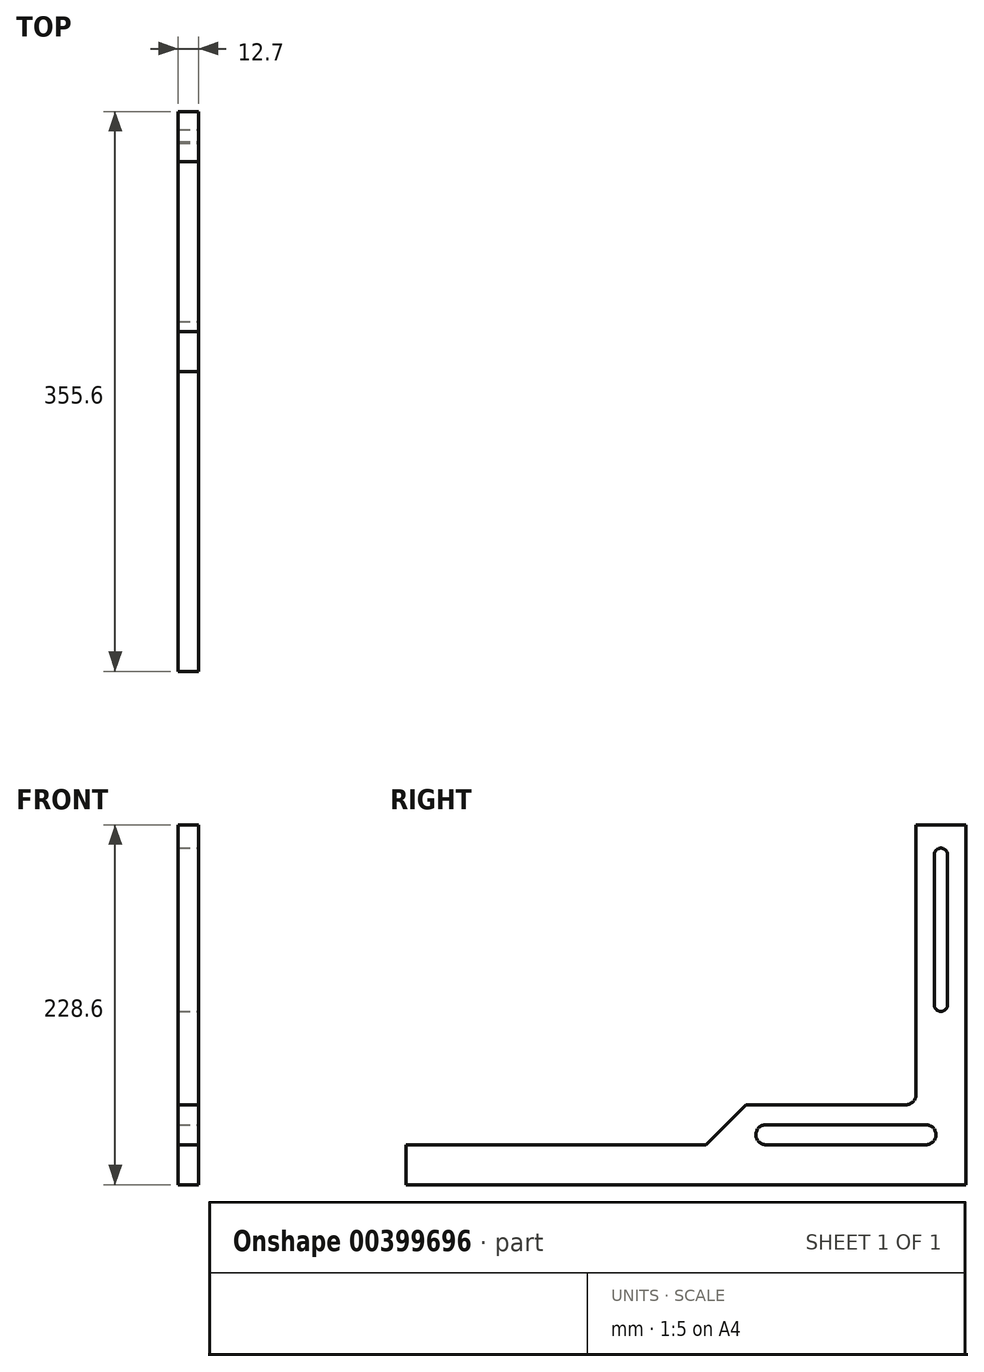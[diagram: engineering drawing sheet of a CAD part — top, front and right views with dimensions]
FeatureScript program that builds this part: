
annotation { "Feature Type Name" : "Feature", "Feature Type Description" : "" }
export const myFeature = defineFeature(function(context is Context, id is Id, definition is map)
    precondition{}
    {
        {
            var Q0;
            Q0=qCreatedBy(makeId("Right.planeOp"),FACE);
            var sketch = newSketch(context, id + "F0", { "sketchPlane" : qUnion([Q0])});
            skLineSegment(sketch, "E0.bottom", {"start": v(-177.8, 25.4) * mm, "end": v(177.8, 25.4) * mm});
            skLineSegment(sketch, "E0.top", {"start": v(-177.8, 0) * mm, "end": v(177.8, 0) * mm});
            skLineSegment(sketch, "E0.left", {"start": v(-177.8, 25.4) * mm, "end": v(-177.8, 0) * mm});
            skLineSegment(sketch, "E0.right", {"start": v(177.8, 25.4) * mm, "end": v(177.8, 0) * mm});
            skLineSegment(sketch, "E1.bottom", {"start": v(177.8, 0) * mm, "end": v(146.05, 0) * mm});
            skLineSegment(sketch, "E1.top", {"start": v(177.8, 228.6) * mm, "end": v(146.05, 228.6) * mm});
            skLineSegment(sketch, "E1.left", {"start": v(177.8, 0) * mm, "end": v(177.8, 228.6) * mm});
            skLineSegment(sketch, "E1.right", {"start": v(146.05, 57.15) * mm, "end": v(146.05, 228.6) * mm});
            skLineSegment(sketch, "E2", {"start": v(139.7, 50.8) * mm, "end": v(38.1, 50.8) * mm});
            skLineSegment(sketch, "E3", {"start": v(38.1, 50.8) * mm, "end": v(12.7, 25.4) * mm});
            skPoint(sketch, "E4.newPointA", {"position": v(146.05, 50.8) * mm});
            skArc(sketch, "E4.filletArc", {"start": v(139.7, 50.8) * mm, "mid": v(144.2, 52.66) * mm, "end": v(146.05, 57.15) * mm});
            skSolve(sketch);
        }
        {
            var Q0;
            {var subQ1=sQuery(id+"F0.wireOp",EDGE,"E0.top");Q0=makeQuery(id+"F0.imprint","IMPRINT",FACE,{"disambiguationData":[TD([[makeQuery(id+"F0.imprint","IMPRINT",EDGE,{"derivedFrom":subQ1}),1.0]])]});}
            var Q1;
            {var subQ4=sQuery(id+"F0.wireOp",EDGE,"E2");Q1=makeQuery(id+"F0.imprint","IMPRINT",FACE,{"disambiguationData":[TD([[makeQuery(id+"F0.imprint","IMPRINT",EDGE,{"derivedFrom":subQ4}),1.0]])]});}
            var Q2;
            {var subQ6=sQuery(id+"F0.wireOp",EDGE,"E1.top");Q2=makeQuery(id+"F0.imprint","IMPRINT",FACE,{"disambiguationData":[TD([[makeQuery(id+"F0.imprint","IMPRINT",EDGE,{"derivedFrom":subQ6}),1.0]])]});}
            var Q3;
            {var subQ5=sQuery(id+"F0.wireOp",EDGE,"E1.bottom");Q3=makeQuery(id+"F0.imprint","IMPRINT",FACE,{"disambiguationData":[TD([[makeQuery(id+"F0.imprint","IMPRINT",EDGE,{"derivedFrom":subQ5}),-1.0]])]});}
            extrude(context, id + "F1", {"entities" : qUnion([Q0, Q1, Q2, Q3]), "depth" : 12.7 * mm});
        }
        {
            var Q0;
            Q0=makeQuery(id+"F1.opExtrude","CAP_FACE",FACE,{"disambiguationData":[OSD([sQuery(id+"F0.wireOp",EDGE,"E0.bottom"),sQuery(id+"F0.wireOp",EDGE,"E0.top"),sQuery(id+"F0.wireOp",EDGE,"E0.left"),sQuery(id+"F0.wireOp",EDGE,"E1.bottom"),sQuery(id+"F0.wireOp",EDGE,"E1.top"),sQuery(id+"F0.wireOp",EDGE,"E1.left"),sQuery(id+"F0.wireOp",EDGE,"E1.right"),sQuery(id+"F0.wireOp",EDGE,"E2"),sQuery(id+"F0.wireOp",EDGE,"E3"),sQuery(id+"F0.wireOp",EDGE,"E4.filletArc")])],"isStart":false});
            var sketch = newSketch(context, id + "F2", { "sketchPlane" : qUnion([Q0])});
            skLineSegment(sketch, "E5", {"start": v(161.92, 228.6) * mm, "end": v(161.92, 0) * mm, "construction": true});
            skLineSegment(sketch, "E6", {"start": v(157.7, 209.55) * mm, "end": v(157.7, 114.3) * mm});
            skLineSegment(sketch, "E7", {"start": v(166.14, 114.3) * mm, "end": v(166.14, 209.55) * mm});
            skArc(sketch, "E8", {"start": v(166.14, 114.3) * mm, "mid": v(161.93, 110.08) * mm, "end": v(157.7, 114.3) * mm});
            skArc(sketch, "E9", {"start": v(166.14, 209.55) * mm, "mid": v(161.92, 213.77) * mm, "end": v(157.7, 209.55) * mm});
            skSolve(sketch);
        }
        {
            var Q0;
            Q0=makeQuery(id+"F2.imprint","IMPRINT",FACE,{"disambiguationData":[TD([[makeQuery(id+"F2.imprint","IMPRINT",EDGE,{"derivedFrom":sQuery(id+"F2.wireOp",EDGE,"E6")}),1.0]])]});
            extrude(context, id + "F3", {"entities" : qUnion([Q0]), "operationType" : NewBodyOperationType.REMOVE, "endBound" : BoundingType.THROUGH_ALL, "oppositeDirection" : true, "depth" : 25.4 * mm});
        }
        {
            var Q0;
            Q0=makeQuery(id+"F1.opExtrude","CAP_FACE",FACE,{"disambiguationData":[OSD([sQuery(id+"F0.wireOp",EDGE,"E0.bottom"),sQuery(id+"F0.wireOp",EDGE,"E0.top"),sQuery(id+"F0.wireOp",EDGE,"E0.left"),sQuery(id+"F0.wireOp",EDGE,"E1.bottom"),sQuery(id+"F0.wireOp",EDGE,"E1.top"),sQuery(id+"F0.wireOp",EDGE,"E1.left"),sQuery(id+"F0.wireOp",EDGE,"E1.right"),sQuery(id+"F0.wireOp",EDGE,"E2"),sQuery(id+"F0.wireOp",EDGE,"E3"),sQuery(id+"F0.wireOp",EDGE,"E4.filletArc")])],"isStart":false});
            var sketch = newSketch(context, id + "F4", { "sketchPlane" : qUnion([Q0])});
            skLineSegment(sketch, "E10", {"start": v(50.8, 38.1) * mm, "end": v(152.4, 38.1) * mm});
            skLineSegment(sketch, "E11", {"start": v(152.4, 25.4) * mm, "end": v(50.8, 25.4) * mm});
            skArc(sketch, "E12", {"start": v(50.8, 38.1) * mm, "mid": v(44.45, 31.75) * mm, "end": v(50.8, 25.4) * mm});
            skArc(sketch, "E13", {"start": v(152.4, 38.1) * mm, "mid": v(158.75, 31.75) * mm, "end": v(152.4, 25.4) * mm});
            skSolve(sketch);
        }
        {
            var Q0;
            Q0=makeQuery(id+"F4.imprint","IMPRINT",FACE,{"disambiguationData":[TD([[makeQuery(id+"F4.imprint","IMPRINT",EDGE,{"derivedFrom":sQuery(id+"F4.wireOp",EDGE,"E10")}),-1.0]])]});
            extrude(context, id + "F5", {"entities" : qUnion([Q0]), "operationType" : NewBodyOperationType.REMOVE, "endBound" : BoundingType.THROUGH_ALL, "oppositeDirection" : true, "depth" : 25.4 * mm});
        }
    });
